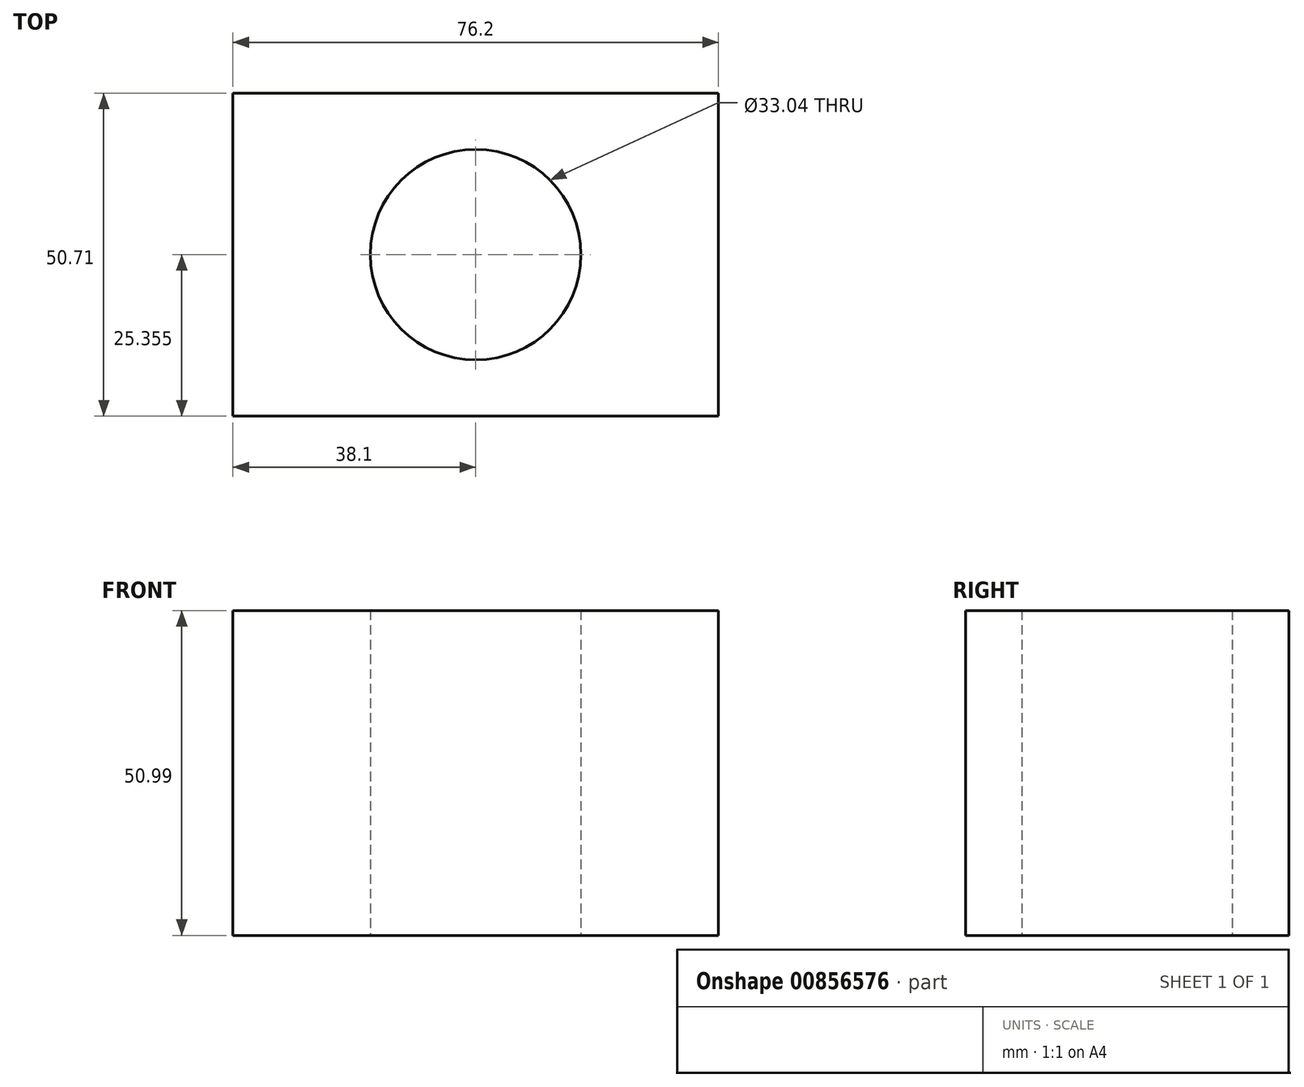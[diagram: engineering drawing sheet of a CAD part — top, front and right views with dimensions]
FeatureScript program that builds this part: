
annotation { "Feature Type Name" : "Feature", "Feature Type Description" : "" }
export const myFeature = defineFeature(function(context is Context, id is Id, definition is map)
    precondition{}
    {
        {
            var Q0;
            Q0=qCreatedBy(makeId("Right.planeOp"),FACE);
            var sketch = newSketch(context, id + "F0", { "sketchPlane" : qUnion([Q0])});
            skLineSegment(sketch, "E0.bottom", {"start": v(-14.8, 30.85) * mm, "end": v(35.92, 30.85) * mm});
            skLineSegment(sketch, "E0.top", {"start": v(-14.8, -20.14) * mm, "end": v(35.92, -20.14) * mm});
            skLineSegment(sketch, "E0.left", {"start": v(-14.8, 30.85) * mm, "end": v(-14.8, -20.14) * mm});
            skLineSegment(sketch, "E0.right", {"start": v(35.92, 30.85) * mm, "end": v(35.92, -20.14) * mm});
            skSolve(sketch);
        }
        {
            var Q0;
            Q0 = qSketchRegion(id + "F0", true);
            extrude(context, id + "F1", {"entities" : qUnion([Q0]), "depth" : 25.4 * mm, "offsetDistance" : 25.4 * mm});
        }
        {
            var Q0;
            Q0=makeQuery(id+"F1.opExtrude","CAP_FACE",FACE,{"disambiguationData":[OSD([sQuery(id+"F0.wireOp",EDGE,"E0.bottom"),sQuery(id+"F0.wireOp",EDGE,"E0.top"),sQuery(id+"F0.wireOp",EDGE,"E0.left"),sQuery(id+"F0.wireOp",EDGE,"E0.right")])],"isStart":false});
            extrude(context, id + "F2", {"entities" : qUnion([Q0]), "operationType" : NewBodyOperationType.ADD, "oppositeDirection" : true, "depth" : 76.2 * mm, "offsetDistance" : 25.4 * mm});
        }
        {
            var Q0;
            {var subQ0=sQuery(id+"F0.wireOp",EDGE,"E0.top");Q0=makeQuery(id+"F2.boolean.opBoolean","MERGE",FACE,{"derivedFrom":[makeQuery(id+"F1.opExtrude","SWEPT_FACE",FACE,{"disambiguationData":[OSD([subQ0])]}),makeQuery(id+"F2.opExtrude","SWEPT_FACE",FACE,{"disambiguationData":[OSD([subQ0])]})]});}
            var sketch = newSketch(context, id + "F3", { "sketchPlane" : qUnion([Q0])});
            skLineSegment(sketch, "E1", {"start": v(-12.7, 14.8) * mm, "end": v(-12.7, -35.92) * mm});
            skLineSegment(sketch, "E2", {"start": v(-50.8, -10.56) * mm, "end": v(25.4, -10.56) * mm});
            skCircle(sketch, "E3", {"center": v(-12.7, -10.56) * mm, "radius": 16.52 * mm});
            skSolve(sketch);
        }
        {
            var Q0;
            Q0 = qSketchRegion(id + "F3", true);
            extrude(context, id + "F4", {"entities" : qUnion([Q0]), "operationType" : NewBodyOperationType.REMOVE, "oppositeDirection" : true, "depth" : 76.2 * mm, "offsetDistance" : 25.4 * mm});
        }
    });
